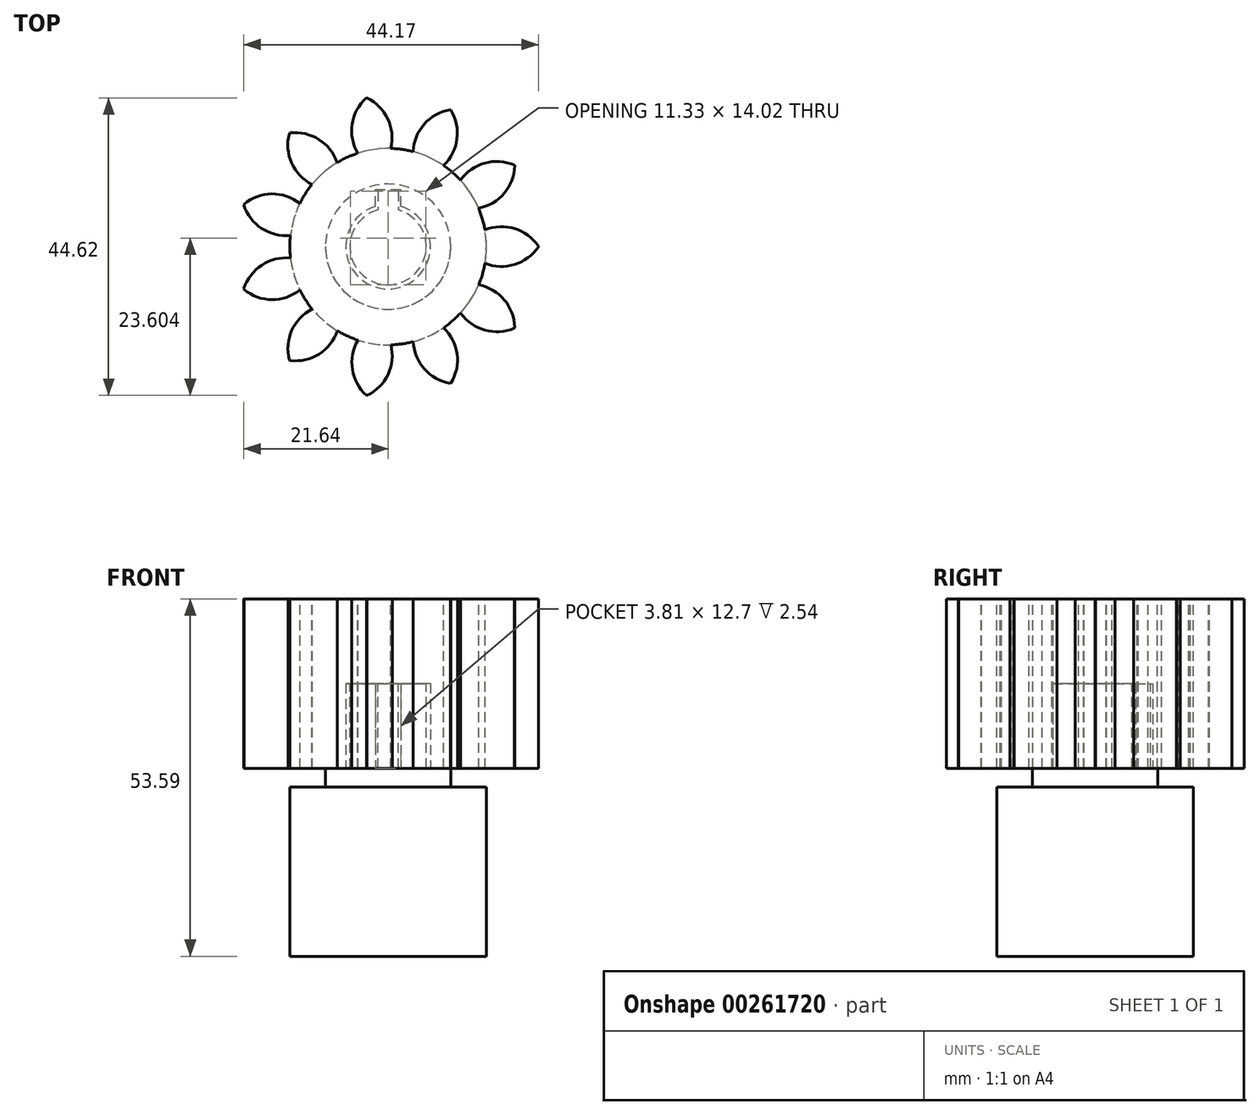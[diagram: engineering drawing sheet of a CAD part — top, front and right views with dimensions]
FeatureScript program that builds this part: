
annotation { "Feature Type Name" : "Feature", "Feature Type Description" : "" }
export const myFeature = defineFeature(function(context is Context, id is Id, definition is map)
    precondition{}
    {
        {
            var Q0;
            Q0=qCreatedBy(makeId("Top.planeOp"),FACE);
            var sketch = newSketch(context, id + "F0", { "sketchPlane" : qUnion([Q0])});
            skCircle(sketch, "E0", {"center": v(0, 0) * mm, "radius": 14.73 * mm});
            skSolve(sketch);
        }
        {
            var Q0;
            Q0=qSketchRegion(id+"F0",true);
            extrude(context, id + "F1", {"entities" : qUnion([Q0]), "depth" : 25.4 * mm});
        }
        {
            var Q0;
            Q0=makeQuery(id+"F1.opExtrude","CAP_FACE",FACE,{"disambiguationData":[OSD([sQuery(id+"F0.wireOp",EDGE,"E0")])],"isStart":false});
            var sketch = newSketch(context, id + "F2", { "sketchPlane" : qUnion([Q0])});
            skCircle(sketch, "E1", {"center": v(0, 0) * mm, "radius": 22.53 * mm, "construction": true});
            skCircle(sketch, "E2", {"center": v(0, 0) * mm, "radius": 19.05 * mm, "construction": true});
            skCircle(sketch, "E3", {"center": v(0, 0) * mm, "radius": 14.7 * mm, "construction": true});
            skLineSegment(sketch, "E4", {"start": v(0, 0) * mm, "end": v(0, 56.9) * mm, "construction": true});
            skLineSegment(sketch, "E5", {"start": v(0, 0) * mm, "end": v(-8.42, 58.23) * mm, "construction": true});
            skLineSegment(sketch, "E6", {"start": v(0, 19.05) * mm, "end": v(-65.71, 19.05) * mm, "construction": true});
            skLineSegment(sketch, "E7", {"start": v(0, 19.05) * mm, "end": v(-58.85, -7.15) * mm, "construction": true});
            skCircle(sketch, "E8", {"center": v(0, 19.05) * mm, "radius": 6.67 * mm, "construction": true});
            skCircle(sketch, "E9", {"center": v(0, 0) * mm, "radius": 17.4 * mm, "construction": true});
            skCircle(sketch, "E10", {"center": v(-6.08, 16.3) * mm, "radius": 6.67 * mm, "construction": true});
            skArc(sketch, "E11", {"start": v(0.4, 14.7) * mm, "mid": v(-0.04, 19.13) * mm, "end": v(-3.17, 22.3) * mm});
            skArc(sketch, "E12.MirrorCS", {"start": v(-4.54, 13.98) * mm, "mid": v(-5.38, 18.36) * mm, "end": v(-3.28, 22.3) * mm});
            skLineSegment(sketch, "E13", {"start": v(-3.28, 22.3) * mm, "end": v(-3.17, 22.3) * mm});
            skLineSegment(sketch, "E14", {"start": v(-4.54, 13.98) * mm, "end": v(0.4, 14.7) * mm});
            skSolve(sketch);
        }
        {
            var Q0;
            Q0=qSketchRegion(id+"F2",true);
            var Q1;
            Q1=makeQuery(id+"F1.opExtrude","CAP_FACE",FACE,{"disambiguationData":[OSD([sQuery(id+"F0.wireOp",EDGE,"E0")])],"isStart":true});
            extrude(context, id + "F3", {"entities" : qUnion([Q0]), "endBound" : BoundingType.UP_TO_SURFACE, "oppositeDirection" : true, "endBoundEntityFace" : qUnion([Q1]), "depth" : 25.4 * mm});
        }
        {
            var Q0;
            Q0=makeQuery(id+"F3.opExtrude","SWEPT_BODY",BODY,{"disambiguationData":[OSD([sQuery(id+"F2.wireOp",EDGE,"E11"),sQuery(id+"F2.wireOp",EDGE,"E12.MirrorCS"),sQuery(id+"F2.wireOp",EDGE,"E13"),sQuery(id+"F2.wireOp",EDGE,"E14")])]});
            var Q1;
            Q1=makeQuery(id+"F1.opExtrude","CAP_EDGE",EDGE,{"disambiguationData":[OSD([sQuery(id+"F0.wireOp",EDGE,"E0")])],"isStart":false});
            circularPattern(context, id + "F4", {"operationType" : NewBodyOperationType.ADD, "entities" : qUnion([Q0]), "axis" : qUnion([Q1]), "angle" : 360 * degree, "instanceCount" : 11, "equalSpace" : true});
        }
        {
            var Q0;
            {var subQ0=makeQuery(id+"F3.opExtrude","CAP_FACE",FACE,{"disambiguationData":[OSD([sQuery(id+"F2.wireOp",EDGE,"E11"),sQuery(id+"F2.wireOp",EDGE,"E12.MirrorCS"),sQuery(id+"F2.wireOp",EDGE,"E13"),sQuery(id+"F2.wireOp",EDGE,"E14")])],"isStart":false});Q0=makeQuery(id+"F4.boolean.opBoolean","MERGE",FACE,{"derivedFrom":[makeQuery(id+"F1.opExtrude","CAP_FACE",FACE,{"disambiguationData":[OSD([sQuery(id+"F0.wireOp",EDGE,"E0")])],"isStart":true}),subQ0,makeQuery(id+"F4.opPattern","COPY",FACE,{"derivedFrom":subQ0,"instanceName":"1"}),makeQuery(id+"F4.opPattern","COPY",FACE,{"derivedFrom":subQ0,"instanceName":"2"}),makeQuery(id+"F4.opPattern","COPY",FACE,{"derivedFrom":subQ0,"instanceName":"3"}),makeQuery(id+"F4.opPattern","COPY",FACE,{"derivedFrom":subQ0,"instanceName":"4"}),makeQuery(id+"F4.opPattern","COPY",FACE,{"derivedFrom":subQ0,"instanceName":"5"}),makeQuery(id+"F4.opPattern","COPY",FACE,{"derivedFrom":subQ0,"instanceName":"6"}),makeQuery(id+"F4.opPattern","COPY",FACE,{"derivedFrom":subQ0,"instanceName":"7"}),makeQuery(id+"F4.opPattern","COPY",FACE,{"derivedFrom":subQ0,"instanceName":"8"}),makeQuery(id+"F4.opPattern","COPY",FACE,{"derivedFrom":subQ0,"instanceName":"9"}),makeQuery(id+"F4.opPattern","COPY",FACE,{"derivedFrom":subQ0,"instanceName":"10"})]});}
            var sketch = newSketch(context, id + "F5", { "sketchPlane" : qUnion([Q0])});
            skArc(sketch, "E15", {"start": v(1.9, -6.06) * mm, "mid": v(0, 6.35) * mm, "end": v(-1.9, -6.06) * mm});
            skLineSegment(sketch, "E16.top", {"start": v(-1.9, -8.6) * mm, "end": v(1.9, -8.6) * mm});
            skLineSegment(sketch, "E16.left", {"start": v(-1.9, -6.06) * mm, "end": v(-1.9, -8.6) * mm});
            skLineSegment(sketch, "E16.right", {"start": v(1.9, -6.06) * mm, "end": v(1.9, -8.6) * mm});
            skPoint(sketch, "E17", {"position": v(0, -8.6) * mm});
            skCircle(sketch, "E18", {"center": v(0, 0) * mm, "radius": 9.52 * mm, "construction": true});
            skSolve(sketch);
        }
        {
            var Q0;
            Q0 = qSketchRegion(id + "F5", true);
            extrude(context, id + "F6", {"entities" : qUnion([Q0]), "operationType" : NewBodyOperationType.REMOVE, "oppositeDirection" : true, "depth" : 12.7 * mm});
        }
        {
            var Q0;
            Q0=makeQuery(id+"F6.boolean.opBoolean","COPY",FACE,{"derivedFrom":makeQuery(id+"F6.opExtrude","CAP_FACE",FACE,{"disambiguationData":[OSD([sQuery(id+"F5.wireOp",EDGE,"E15"),sQuery(id+"F5.wireOp",EDGE,"E16.top"),sQuery(id+"F5.wireOp",EDGE,"E16.left"),sQuery(id+"F5.wireOp",EDGE,"E16.right")])],"isStart":false})});
            var sketch = newSketch(context, id + "F7", { "sketchPlane" : qUnion([Q0])});
            skArc(sketch, "E19", {"start": v(1.52, -5.5) * mm, "mid": v(0, 5.72) * mm, "end": v(-1.52, -5.5) * mm});
            skPoint(sketch, "E20.endSnap0", {"position": v(-1.9, -7.33) * mm});
            skPoint(sketch, "E21.endSnap0", {"position": v(1.9, -7.33) * mm});
            skLineSegment(sketch, "E22.top", {"start": v(-1.52, -8.3) * mm, "end": v(1.52, -8.3) * mm});
            skLineSegment(sketch, "E22.left", {"start": v(-1.52, -5.5) * mm, "end": v(-1.52, -8.3) * mm});
            skLineSegment(sketch, "E22.right", {"start": v(1.52, -5.5) * mm, "end": v(1.52, -8.3) * mm});
            skPoint(sketch, "E23", {"position": v(0, -8.3) * mm});
            skSolve(sketch);
        }
        {
            var Q0;
            Q0 = qSketchRegion(id + "F7", true);
            var Q1;
            {var subQ0=makeQuery(id+"F3.opExtrude","CAP_FACE",FACE,{"disambiguationData":[OSD([sQuery(id+"F2.wireOp",EDGE,"E11"),sQuery(id+"F2.wireOp",EDGE,"E12.MirrorCS"),sQuery(id+"F2.wireOp",EDGE,"E13"),sQuery(id+"F2.wireOp",EDGE,"E14")])],"isStart":false});Q1=makeQuery(id+"F4.boolean.opBoolean","MERGE",FACE,{"derivedFrom":[makeQuery(id+"F1.opExtrude","CAP_FACE",FACE,{"disambiguationData":[OSD([sQuery(id+"F0.wireOp",EDGE,"E0")])],"isStart":true}),subQ0,makeQuery(id+"F4.opPattern","COPY",FACE,{"derivedFrom":subQ0,"instanceName":"1"}),makeQuery(id+"F4.opPattern","COPY",FACE,{"derivedFrom":subQ0,"instanceName":"2"}),makeQuery(id+"F4.opPattern","COPY",FACE,{"derivedFrom":subQ0,"instanceName":"3"}),makeQuery(id+"F4.opPattern","COPY",FACE,{"derivedFrom":subQ0,"instanceName":"4"}),makeQuery(id+"F4.opPattern","COPY",FACE,{"derivedFrom":subQ0,"instanceName":"5"}),makeQuery(id+"F4.opPattern","COPY",FACE,{"derivedFrom":subQ0,"instanceName":"6"}),makeQuery(id+"F4.opPattern","COPY",FACE,{"derivedFrom":subQ0,"instanceName":"7"}),makeQuery(id+"F4.opPattern","COPY",FACE,{"derivedFrom":subQ0,"instanceName":"8"}),makeQuery(id+"F4.opPattern","COPY",FACE,{"derivedFrom":subQ0,"instanceName":"9"}),makeQuery(id+"F4.opPattern","COPY",FACE,{"derivedFrom":subQ0,"instanceName":"10"})]});}
            extrude(context, id + "F8", {"entities" : qUnion([Q0]), "endBound" : BoundingType.UP_TO_SURFACE, "endBoundEntityFace" : qUnion([Q1]), "depth" : 12.7 * mm});
        }
        {
            var Q0;
            Q0=makeQuery(id+"F8.opExtrude","CAP_FACE",FACE,{"disambiguationData":[OSD([sQuery(id+"F7.wireOp",EDGE,"E19"),sQuery(id+"F7.wireOp",EDGE,"E22.top"),sQuery(id+"F7.wireOp",EDGE,"E22.left"),sQuery(id+"F7.wireOp",EDGE,"E22.right")])],"isStart":false});
            var sketch = newSketch(context, id + "F9", { "sketchPlane" : qUnion([Q0])});
            skCircle(sketch, "E24", {"center": v(0, 0) * mm, "radius": 9.4 * mm});
            skSolve(sketch);
        }
        {
            var Q0;
            Q0 = qSketchRegion(id + "F9", true);
            extrude(context, id + "F10", {"entities" : qUnion([Q0]), "operationType" : NewBodyOperationType.ADD, "depth" : 2.8 * mm});
        }
        {
            var Q0;
            Q0=makeQuery(id+"F10.opExtrude","CAP_FACE",FACE,{"disambiguationData":[OSD([sQuery(id+"F9.wireOp",EDGE,"E24")])],"isStart":false});
            var sketch = newSketch(context, id + "F11", { "sketchPlane" : qUnion([Q0])});
            skCircle(sketch, "E25", {"center": v(0, 0) * mm, "radius": 14.73 * mm});
            skSolve(sketch);
        }
        {
            var Q0;
            Q0 = qSketchRegion(id + "F11", true);
            extrude(context, id + "F12", {"entities" : qUnion([Q0]), "operationType" : NewBodyOperationType.ADD, "depth" : 25.4 * mm});
        }
    });
